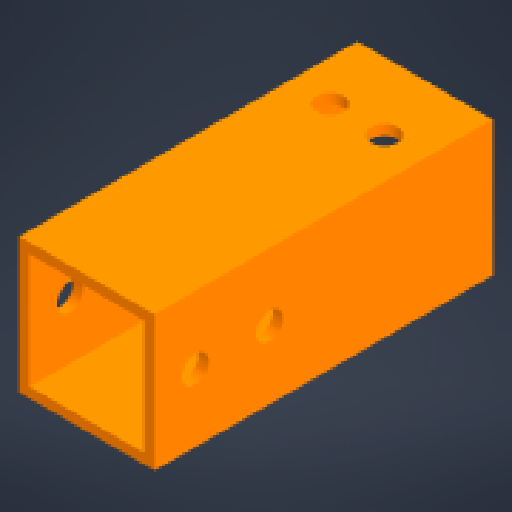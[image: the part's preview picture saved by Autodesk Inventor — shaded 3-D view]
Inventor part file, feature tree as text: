
AUTODESK INVENTOR PART (.ipt)
format: ipt  version: 2024 (Build 280153000, 153)  size: 166,912 bytes
history: native  units: mm
features: extrude x4, sketch x4, other x3, reference x1
ambient origin geometry x8: Origin, YZ Plane, XZ Plane, XY Plane, X Axis, Y Axis, Z Axis, Center Point
bodies: Body1 (feature_tree)
feature tree (12):
  extrude  "Выдавливание3"  Depth=20.0mm TaperAngle=0.0deg
  extrude  "Выдавливание4"  Depth=4.0mm
  extrude  "Выдавливание5"  TaperAngle=0.0deg  [1 undecoded]
  extrude  "Выдавливание6"  Depth=6.0mm
  sketch  "Эскиз5"
  sketch  "Эскиз6"
  sketch  "Эскиз7"
  sketch  "Эскиз8"
  reference  "Ссылка2"
  parser-record x1  (decoder bookkeeping rows leaked as tree rows — omitted from the tree; the rows remain in map.json)
  other  "base_assembly.iam"
  other  "DIN 125-1 A A 4,3:2"
note: 1 required parameter value undecoded (feature->parameter linkage not recoverable at this tier; creation-order binding heuristic only, values carry confidence <= 0.55)
note: 1 file-system path scrubbed to <path> (originals preserved in map.json)
